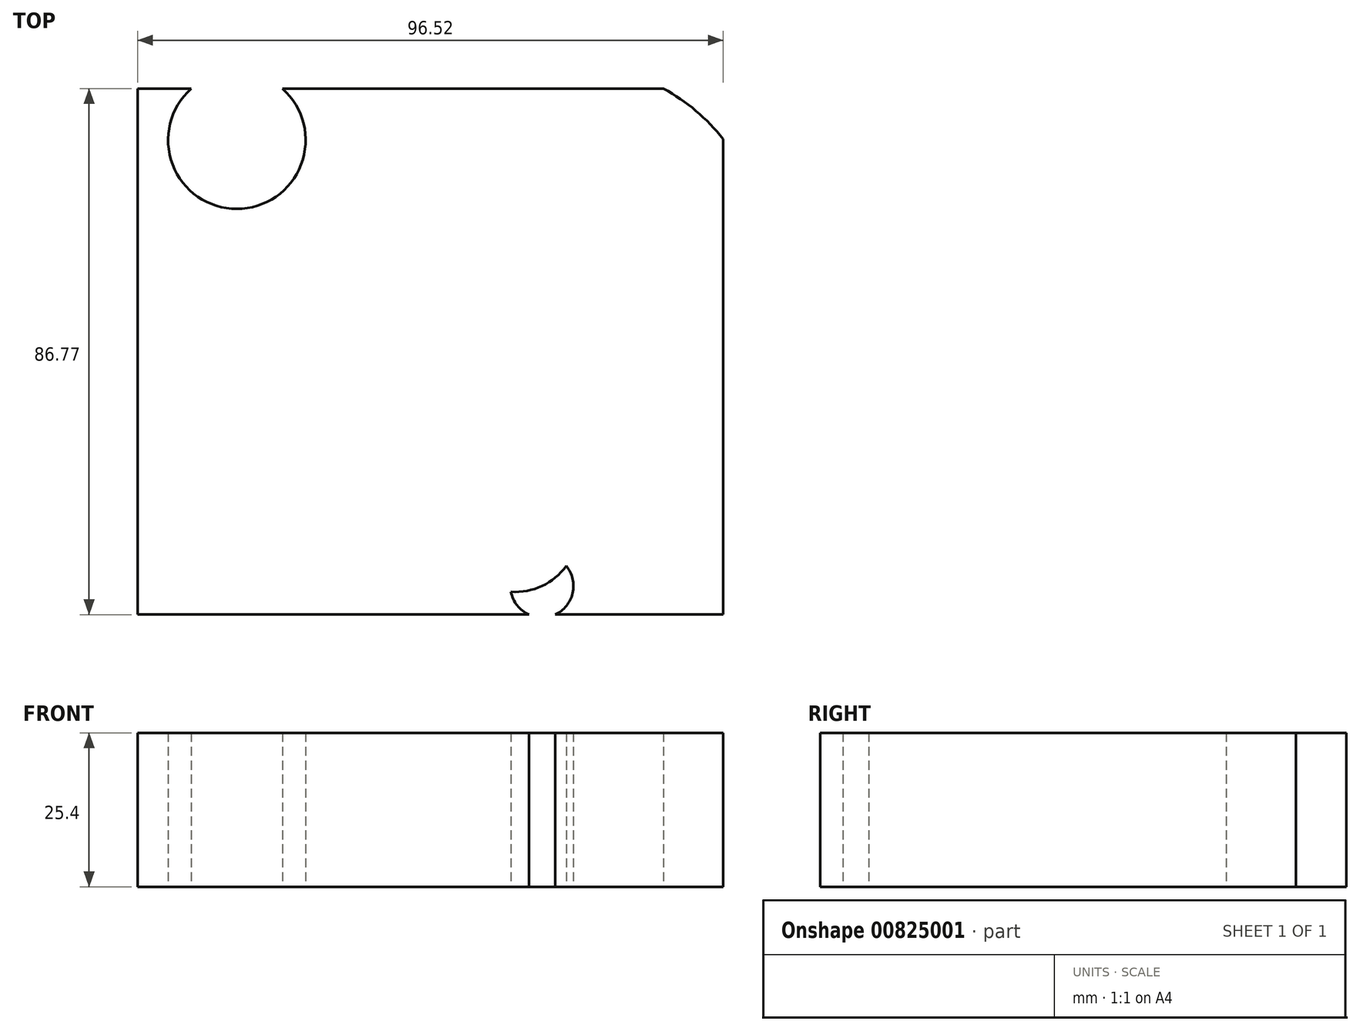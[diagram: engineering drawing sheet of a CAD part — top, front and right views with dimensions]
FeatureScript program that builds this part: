
annotation { "Feature Type Name" : "Feature", "Feature Type Description" : "" }
export const myFeature = defineFeature(function(context is Context, id is Id, definition is map)
    precondition{}
    {
        {
            var Q0;
            Q0=qCreatedBy(makeId("Top.planeOp"),FACE);
            var sketch = newSketch(context, id + "F0", { "sketchPlane" : qUnion([Q0])});
            skLineSegment(sketch, "E0.bottom", {"start": v(-41.66, 42.44) * mm, "end": v(54.86, 42.44) * mm});
            skLineSegment(sketch, "E0.top", {"start": v(-41.66, -44.33) * mm, "end": v(54.86, -44.33) * mm});
            skLineSegment(sketch, "E0.left", {"start": v(-41.66, 42.44) * mm, "end": v(-41.66, -44.33) * mm});
            skLineSegment(sketch, "E0.right", {"start": v(54.86, 42.44) * mm, "end": v(54.86, -44.33) * mm});
            skCircle(sketch, "E1", {"center": v(-25.3, 33.95) * mm, "radius": 11.34 * mm});
            skCircle(sketch, "E2", {"center": v(28.14, 22.95) * mm, "radius": 8.39 * mm});
            skCircle(sketch, "E3", {"center": v(30.02, 14.78) * mm, "radius": 31.48 * mm});
            skCircle(sketch, "E4", {"center": v(20.6, -30.18) * mm, "radius": 10.4 * mm});
            skCircle(sketch, "E5", {"center": v(25, -39.61) * mm, "radius": 5.18 * mm});
            skCircle(sketch, "E6", {"center": v(-27.5, -21.06) * mm, "radius": 6.77 * mm});
            skCircle(sketch, "E7", {"center": v(-6.76, -11.95) * mm, "radius": 8.35 * mm});
            skCircle(sketch, "E8", {"center": v(-14.62, 17.92) * mm, "radius": 6.1 * mm});
            skSolve(sketch);
        }
        {
            var Q0;
            {var subQ9=sQuery(id+"F0.wireOp",EDGE,"E0.left");Q0=makeQuery(id+"F0.imprint","IMPRINT",FACE,{"disambiguationData":[TD([[makeQuery(id+"F0.imprint","IMPRINT",EDGE,{"derivedFrom":subQ9}),1.0]])]});}
            var Q1;
            {var subQ0=sQuery(id+"F0.wireOp",EDGE,"E1");var subQ1=sQuery(id+"F0.wireOp",EDGE,"E0.bottom");var subQ2=makeQuery(id+"F0.imprint","INTERSECT",VERTEX,{"disambiguationData":[OD(0.0)],"derivedFrom":[subQ1,subQ0]});Q1=makeQuery(id+"F0.imprint","IMPRINT",FACE,{"disambiguationData":[TD([[makeQuery(id+"F0.imprint","IMPRINT",EDGE,{"disambiguationData":[TD([[subQ2,-1.0]])],"derivedFrom":subQ1}),-1.0]])]});}
            var Q2;
            Q2=makeQuery(id+"F0.imprint","IMPRINT",FACE,{"disambiguationData":[TD([[makeQuery(id+"F0.imprint","IMPRINT",EDGE,{"derivedFrom":sQuery(id+"F0.wireOp",EDGE,"E6")}),1.0]])]});
            var Q3;
            Q3=makeQuery(id+"F0.imprint","IMPRINT",FACE,{"disambiguationData":[TD([[makeQuery(id+"F0.imprint","IMPRINT",EDGE,{"derivedFrom":sQuery(id+"F0.wireOp",EDGE,"E2")}),-1.0]])]});
            var Q4;
            Q4=makeQuery(id+"F0.imprint","IMPRINT",FACE,{"disambiguationData":[TD([[makeQuery(id+"F0.imprint","IMPRINT",EDGE,{"derivedFrom":sQuery(id+"F0.wireOp",EDGE,"E2")}),1.0]])]});
            var Q5;
            {var subQ0=sQuery(id+"F0.wireOp",EDGE,"E5");var subQ1=sQuery(id+"F0.wireOp",EDGE,"E4");var subQ2=makeQuery(id+"F0.imprint","INTERSECT",VERTEX,{"disambiguationData":[OD(0.0)],"derivedFrom":[subQ1,subQ0]});Q5=makeQuery(id+"F0.imprint","IMPRINT",FACE,{"disambiguationData":[TD([[makeQuery(id+"F0.imprint","IMPRINT",EDGE,{"disambiguationData":[TD([[subQ2,1.0]])],"derivedFrom":subQ1}),1.0]])]});}
            var Q6;
            {var subQ0=sQuery(id+"F0.wireOp",EDGE,"E5");var subQ1=sQuery(id+"F0.wireOp",EDGE,"E0.top");var subQ2=makeQuery(id+"F0.imprint","INTERSECT",VERTEX,{"disambiguationData":[OD(0.0)],"derivedFrom":[subQ1,subQ0]});Q6=makeQuery(id+"F0.imprint","IMPRINT",FACE,{"disambiguationData":[TD([[makeQuery(id+"F0.imprint","IMPRINT",EDGE,{"disambiguationData":[TD([[subQ2,-1.0]])],"derivedFrom":subQ1}),1.0]])]});}
            var Q7;
            Q7=makeQuery(id+"F0.imprint","IMPRINT",FACE,{"disambiguationData":[TD([[makeQuery(id+"F0.imprint","IMPRINT",EDGE,{"derivedFrom":sQuery(id+"F0.wireOp",EDGE,"E7")}),1.0]])]});
            var Q8;
            {var subQ0=sQuery(id+"F0.wireOp",EDGE,"E5");var subQ1=sQuery(id+"F0.wireOp",EDGE,"E4");var subQ2=makeQuery(id+"F0.imprint","INTERSECT",VERTEX,{"disambiguationData":[OD(0.0)],"derivedFrom":[subQ1,subQ0]});Q8=makeQuery(id+"F0.imprint","IMPRINT",FACE,{"disambiguationData":[TD([[makeQuery(id+"F0.imprint","IMPRINT",EDGE,{"disambiguationData":[TD([[subQ2,-1.0]])],"derivedFrom":subQ1}),1.0]])]});}
            var Q9;
            Q9=makeQuery(id+"F0.imprint","IMPRINT",FACE,{"disambiguationData":[TD([[makeQuery(id+"F0.imprint","IMPRINT",EDGE,{"derivedFrom":sQuery(id+"F0.wireOp",EDGE,"E8")}),1.0]])]});
            extrude(context, id + "F1", {"entities" : qUnion([Q0, Q1, Q2, Q3, Q4, Q5, Q6, Q7, Q8, Q9]), "depth" : 25.4 * mm, "offsetDistance" : 25.4 * mm});
        }
    });
